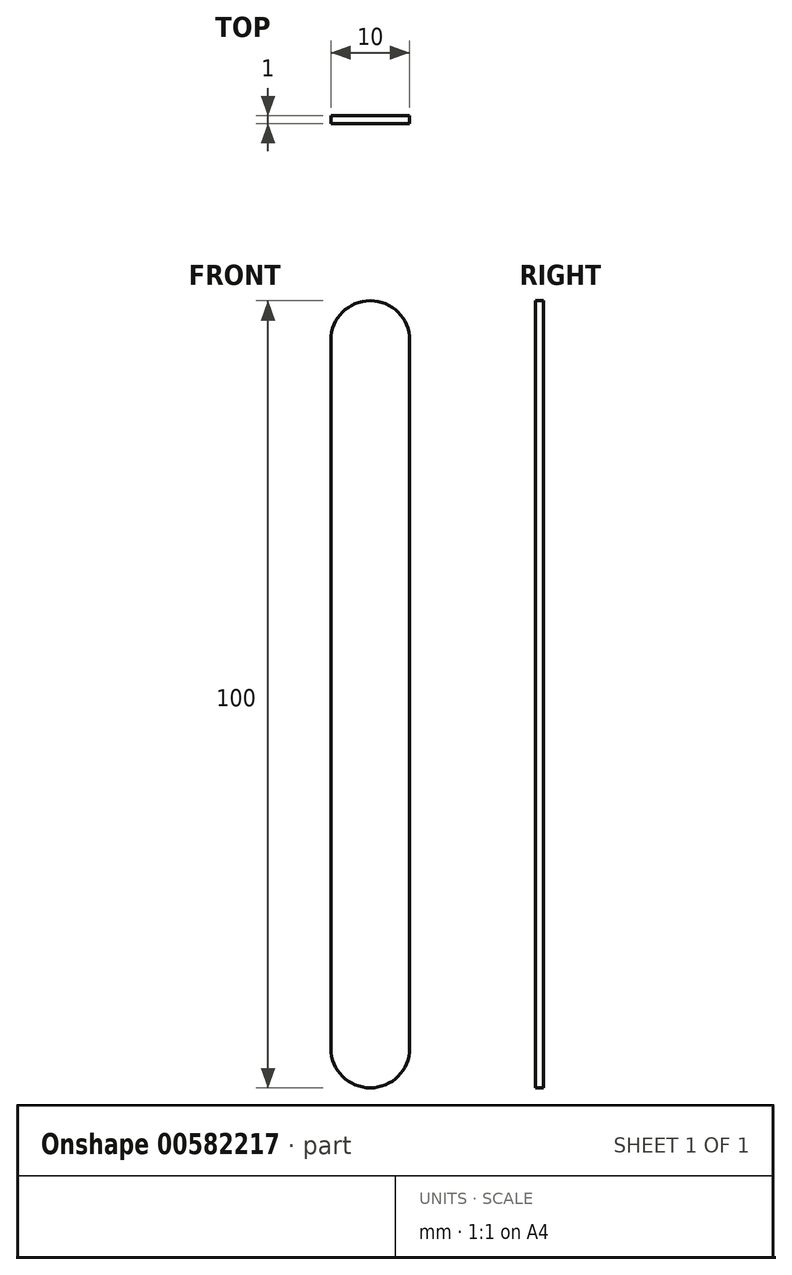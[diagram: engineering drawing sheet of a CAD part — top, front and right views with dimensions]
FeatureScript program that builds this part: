
annotation { "Feature Type Name" : "Feature", "Feature Type Description" : "" }
export const myFeature = defineFeature(function(context is Context, id is Id, definition is map)
    precondition{}
    {
        {
            var Q0;
            Q0=qCreatedBy(makeId("Front.planeOp"),FACE);
            var sketch = newSketch(context, id + "F0", { "sketchPlane" : qUnion([Q0])});
            skLineSegment(sketch, "E0.bottom", {"start": v(0, 0) * mm, "end": v(10, 0) * mm});
            skLineSegment(sketch, "E0.top", {"start": v(0, 100) * mm, "end": v(10, 100) * mm});
            skLineSegment(sketch, "E0.left", {"start": v(0, 0) * mm, "end": v(0, 100) * mm});
            skLineSegment(sketch, "E0.right", {"start": v(10, 0) * mm, "end": v(10, 100) * mm});
            skSolve(sketch);
        }
        {
            var Q0;
            Q0=makeQuery(id+"F0.imprint","IMPRINT",FACE,{"disambiguationData":[TD([[makeQuery(id+"F0.imprint","IMPRINT",EDGE,{"derivedFrom":sQuery(id+"F0.wireOp",EDGE,"E0.bottom")}),1.0]])]});
            extrude(context, id + "F1", {"entities" : qUnion([Q0]), "endBound" : BoundingType.SYMMETRIC, "depth" : 1 * mm, "offsetDistance" : 25 * mm});
        }
        {
            var Q0;
            Q0=makeQuery(id+"F1.opExtrude","SWEPT_EDGE",EDGE,{"disambiguationData":[OSD([sQuery(id+"F0.wireOp",EDGE,"E0.top"),sQuery(id+"F0.wireOp",EDGE,"E0.left")])]});
            fillet(context, id + "F2", {"entities" : qUnion([Q0]), "radius" : 5 * mm, "tangentPropagation" : true, "allowEdgeOverflow" : false});
        }
        {
            var Q0;
            Q0=makeQuery(id+"F1.opExtrude","SWEPT_EDGE",EDGE,{"disambiguationData":[OSD([sQuery(id+"F0.wireOp",EDGE,"E0.top"),sQuery(id+"F0.wireOp",EDGE,"E0.right")])]});
            fillet(context, id + "F3", {"entities" : qUnion([Q0]), "radius" : 5 * mm, "tangentPropagation" : true, "allowEdgeOverflow" : false});
        }
        {
            var Q0;
            Q0=makeQuery(id+"F1.opExtrude","SWEPT_EDGE",EDGE,{"disambiguationData":[OSD([sQuery(id+"F0.wireOp",EDGE,"E0.bottom"),sQuery(id+"F0.wireOp",EDGE,"E0.left")])]});
            fillet(context, id + "F4", {"entities" : qUnion([Q0]), "radius" : 5 * mm, "tangentPropagation" : true, "allowEdgeOverflow" : false});
        }
        {
            var Q0;
            Q0=makeQuery(id+"F1.opExtrude","SWEPT_EDGE",EDGE,{"disambiguationData":[OSD([sQuery(id+"F0.wireOp",EDGE,"E0.bottom"),sQuery(id+"F0.wireOp",EDGE,"E0.right")])]});
            fillet(context, id + "F5", {"entities" : qUnion([Q0]), "radius" : 5 * mm, "tangentPropagation" : true, "allowEdgeOverflow" : false});
        }
    });
